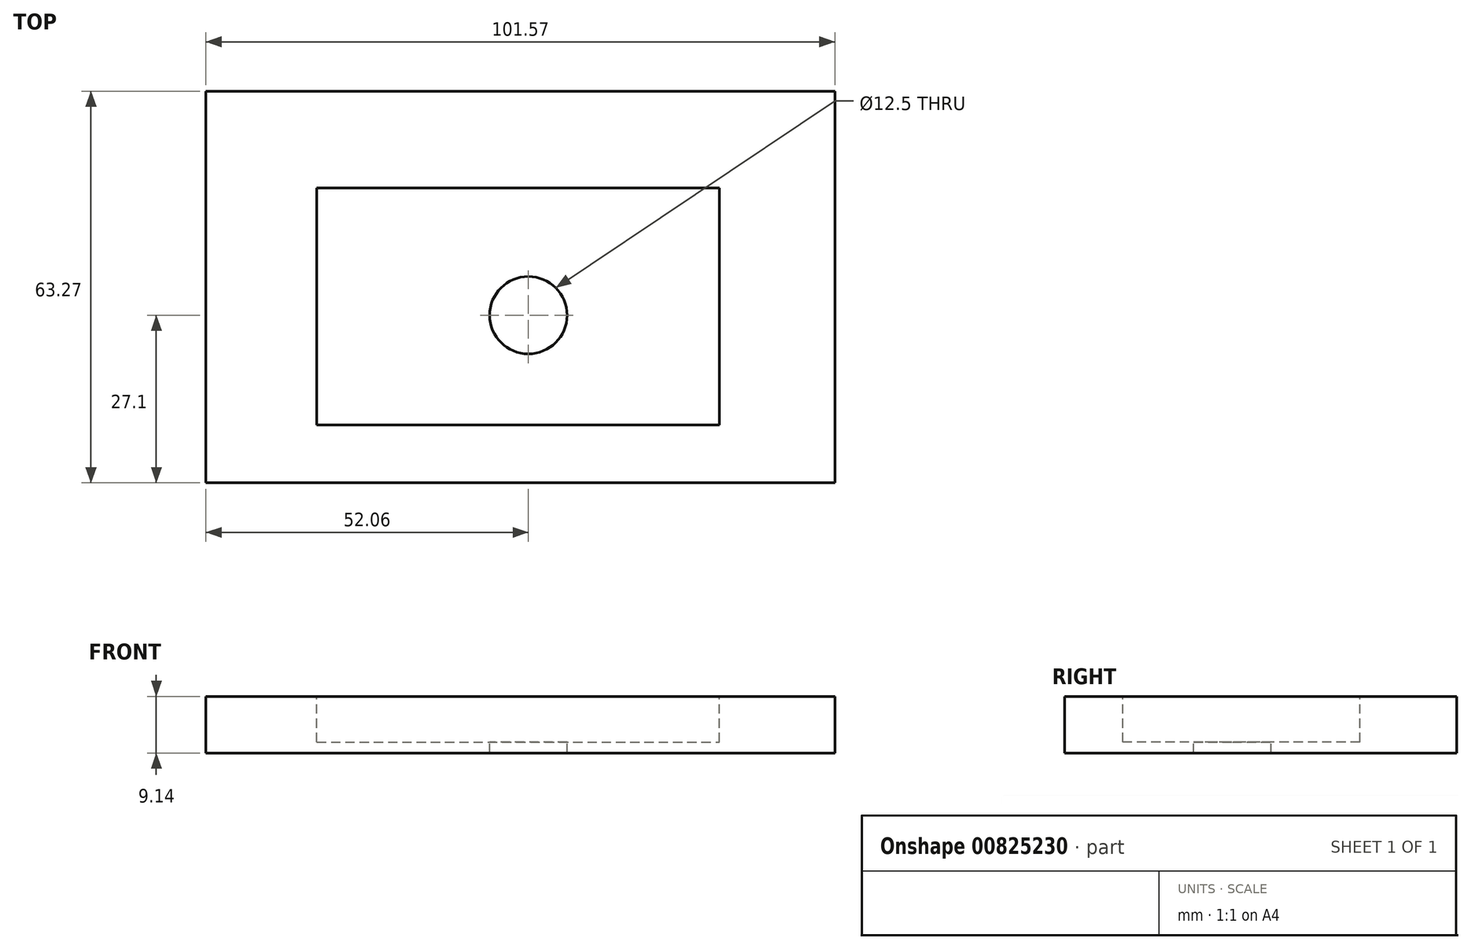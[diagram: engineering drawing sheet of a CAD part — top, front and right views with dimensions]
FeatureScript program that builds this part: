
annotation { "Feature Type Name" : "Feature", "Feature Type Description" : "" }
export const myFeature = defineFeature(function(context is Context, id is Id, definition is map)
    precondition{}
    {
        {
            var Q0;
            Q0=qCreatedBy(makeId("Top.planeOp"),FACE);
            var sketch = newSketch(context, id + "F0", { "sketchPlane" : qUnion([Q0])});
            skLineSegment(sketch, "E0", {"start": v(0, 36.17) * mm, "end": v(-52.06, 36.17) * mm});
            skLineSegment(sketch, "E1", {"start": v(-52.06, 36.17) * mm, "end": v(-52.06, -27.1) * mm});
            skLineSegment(sketch, "E2", {"start": v(-52.06, -27.1) * mm, "end": v(49.5, -27.1) * mm});
            skLineSegment(sketch, "E3", {"start": v(49.5, -27.1) * mm, "end": v(49.5, 36.17) * mm});
            skLineSegment(sketch, "E4", {"start": v(49.5, 36.17) * mm, "end": v(0, 36.17) * mm});
            skSolve(sketch);
        }
        {
            var Q0;
            Q0 = qSketchRegion(id + "F0", true);
            extrude(context, id + "F1", {"entities" : qUnion([Q0]), "oppositeDirection" : true, "depth" : 9.14 * mm, "offsetDistance" : 25.4 * mm});
        }
        {
            var Q0;
            Q0=qCreatedBy(makeId("Top.planeOp"),FACE);
            var sketch = newSketch(context, id + "F2", { "sketchPlane" : qUnion([Q0])});
            skLineSegment(sketch, "E5.bottom", {"start": v(-34.15, 20.57) * mm, "end": v(30.82, 20.57) * mm});
            skLineSegment(sketch, "E5.top", {"start": v(-34.15, -17.73) * mm, "end": v(30.82, -17.73) * mm});
            skLineSegment(sketch, "E5.left", {"start": v(-34.15, 20.57) * mm, "end": v(-34.15, -17.73) * mm});
            skLineSegment(sketch, "E5.right", {"start": v(30.82, 20.57) * mm, "end": v(30.82, -17.73) * mm});
            skSolve(sketch);
        }
        {
            var Q0;
            Q0 = qSketchRegion(id + "F2", true);
            extrude(context, id + "F3", {"entities" : qUnion([Q0]), "operationType" : NewBodyOperationType.REMOVE, "oppositeDirection" : true, "depth" : 7.37 * mm, "offsetDistance" : 25.4 * mm});
        }
        {
            var Q0;
            Q0=qCreatedBy(makeId("Top.planeOp"),FACE);
            var sketch = newSketch(context, id + "F4", { "sketchPlane" : qUnion([Q0])});
            skCircle(sketch, "E6", {"center": v(0, 0) * mm, "radius": 6.99 * mm});
            skSolve(sketch);
        }
        {
            var Q0;
            Q0=sQuery(id+"F4.wireOp",VERTEX,"E6.center");
            var Q1;
            Q1=makeQuery(id+"F1.opExtrude","SWEPT_BODY",BODY,{"disambiguationData":[OSD([sQuery(id+"F0.wireOp",EDGE,"E0"),sQuery(id+"F0.wireOp",EDGE,"E1"),sQuery(id+"F0.wireOp",EDGE,"E2"),sQuery(id+"F0.wireOp",EDGE,"E3"),sQuery(id+"F0.wireOp",EDGE,"E4")])]});
            hole(context, id + "F5", {"style" : HoleStyle.SIMPLE, "endStyle" : HoleEndStyle.THROUGH, "holeDiameter" : 12.5 * mm, "majorDiameter" : 6.35 * mm, "isTappedThrough" : true, "tappedDepth" : 12.7 * mm, "tapClearance" : 3, "locations" : qUnion([Q0]), "scope" : qUnion([Q1])});
        }
    });
